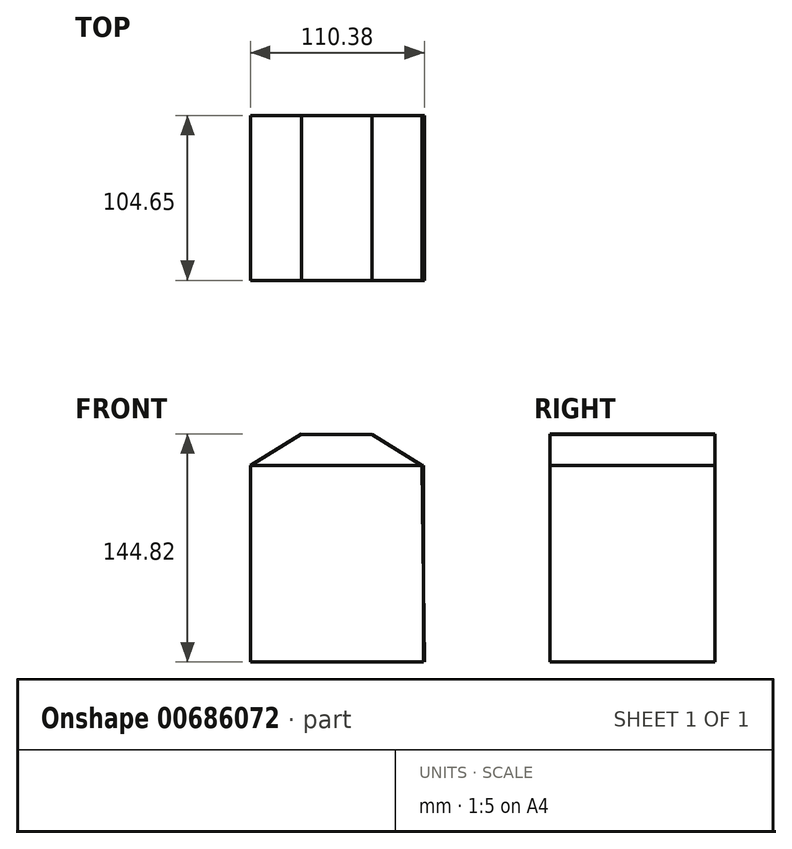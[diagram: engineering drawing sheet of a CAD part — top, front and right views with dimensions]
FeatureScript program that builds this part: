
annotation { "Feature Type Name" : "Feature", "Feature Type Description" : "" }
export const myFeature = defineFeature(function(context is Context, id is Id, definition is map)
    precondition{}
    {
        {
            var Q0;
            Q0=qCreatedBy(makeId("Front.planeOp"),FACE);
            var sketch = newSketch(context, id + "F0", { "sketchPlane" : qUnion([Q0])});
            skLineSegment(sketch, "E0", {"start": v(-51.32, -75.76) * mm, "end": v(-51.32, 48.97) * mm});
            skLineSegment(sketch, "E1", {"start": v(57.65, 48.97) * mm, "end": v(59.06, -75.63) * mm});
            skLineSegment(sketch, "E2", {"start": v(-51.32, 48.97) * mm, "end": v(-18.92, 69.06) * mm});
            skLineSegment(sketch, "E3", {"start": v(57.65, 48.97) * mm, "end": v(25.8, 68.7) * mm});
            skLineSegment(sketch, "E4", {"start": v(25.8, 68.7) * mm, "end": v(-18.92, 68.7) * mm});
            skSolve(sketch);
        }
        {
            var Q0;
            Q0=sQuery(id+"F0.wireOp",EDGE,"E0");
            var Q1;
            Q1=sQuery(id+"F0.wireOp",EDGE,"E2");
            var Q2;
            Q2=sQuery(id+"F0.wireOp",EDGE,"E4");
            var Q3;
            Q3=sQuery(id+"F0.wireOp",EDGE,"E3");
            var Q4;
            Q4=sQuery(id+"F0.wireOp",EDGE,"E1");
            extrude(context, id + "F1", {"bodyType" : ToolBodyType.SURFACE, "surfaceEntities" : qUnion([Q0, Q1, Q2, Q3, Q4]), "depth" : 104.65 * mm, "offsetDistance" : 25.4 * mm});
        }
        {
            var Q0;
            Q0=makeQuery(id+"F1.opExtrude","SWEPT_FACE",FACE,{"disambiguationData":[OSD([sQuery(id+"F0.wireOp",EDGE,"E0")])]});
            var sketch = newSketch(context, id + "F2", { "sketchPlane" : qUnion([Q0])});
            skLineSegment(sketch, "E5", {"start": v(0, 48.97) * mm, "end": v(0, -75.76) * mm});
            skSolve(sketch);
        }
        {
            var Q0;
            Q0=sQuery(id+"F2.wireOp",EDGE,"E5");
            extrude(context, id + "F3", {"bodyType" : ToolBodyType.SURFACE, "surfaceEntities" : qUnion([Q0]), "depth" : 109.98 * mm, "offsetDistance" : 25.4 * mm});
        }
    });
